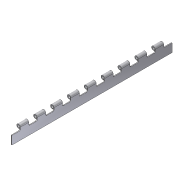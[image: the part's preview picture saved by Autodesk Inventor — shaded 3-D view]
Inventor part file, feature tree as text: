
AUTODESK INVENTOR PART (.ipt)
format: ipt  version: unknown  size: 326,144 bytes
history: native  units: in
note: dims shown in document units (in); Inventor stores cm internally (conversion verified against a paired STEP export)
features: extrude x2, sketch x2, pattern_linear x1, fillet x1, projected_geometry x1
ambient origin geometry x8: Origin, YZ Plane, XZ Plane, XY Plane, X Axis, Y Axis, Z Axis, Center Point
feature tree (7):
  extrude  "Extrusion1"  Depth=0.09in
  extrude  "Extrusion2"  Depth=19.0in TaperAngle=0.0deg
  pattern_linear  "Rectangular Pattern1"  Spacing1=1.0in  [1 undecoded]
  fillet  "Fillet2"  Radius=0.125in
  sketch  "Sketch1"  dims[d0=0.445in d1=0.09in]
  sketch  "Sketch2"  dims[d2=0.09in d3=19.0in d4=0.0in d6=1.0in d7=0.125in d8=16.0in d9=0.0in d11=3.937in d13=2.0in d14=0.125in]
  projected_geometry  "Projected Loop1"
note: 1 required parameter value undecoded (feature->parameter linkage not recoverable at this tier; creation-order binding heuristic only, values carry confidence <= 0.55)
